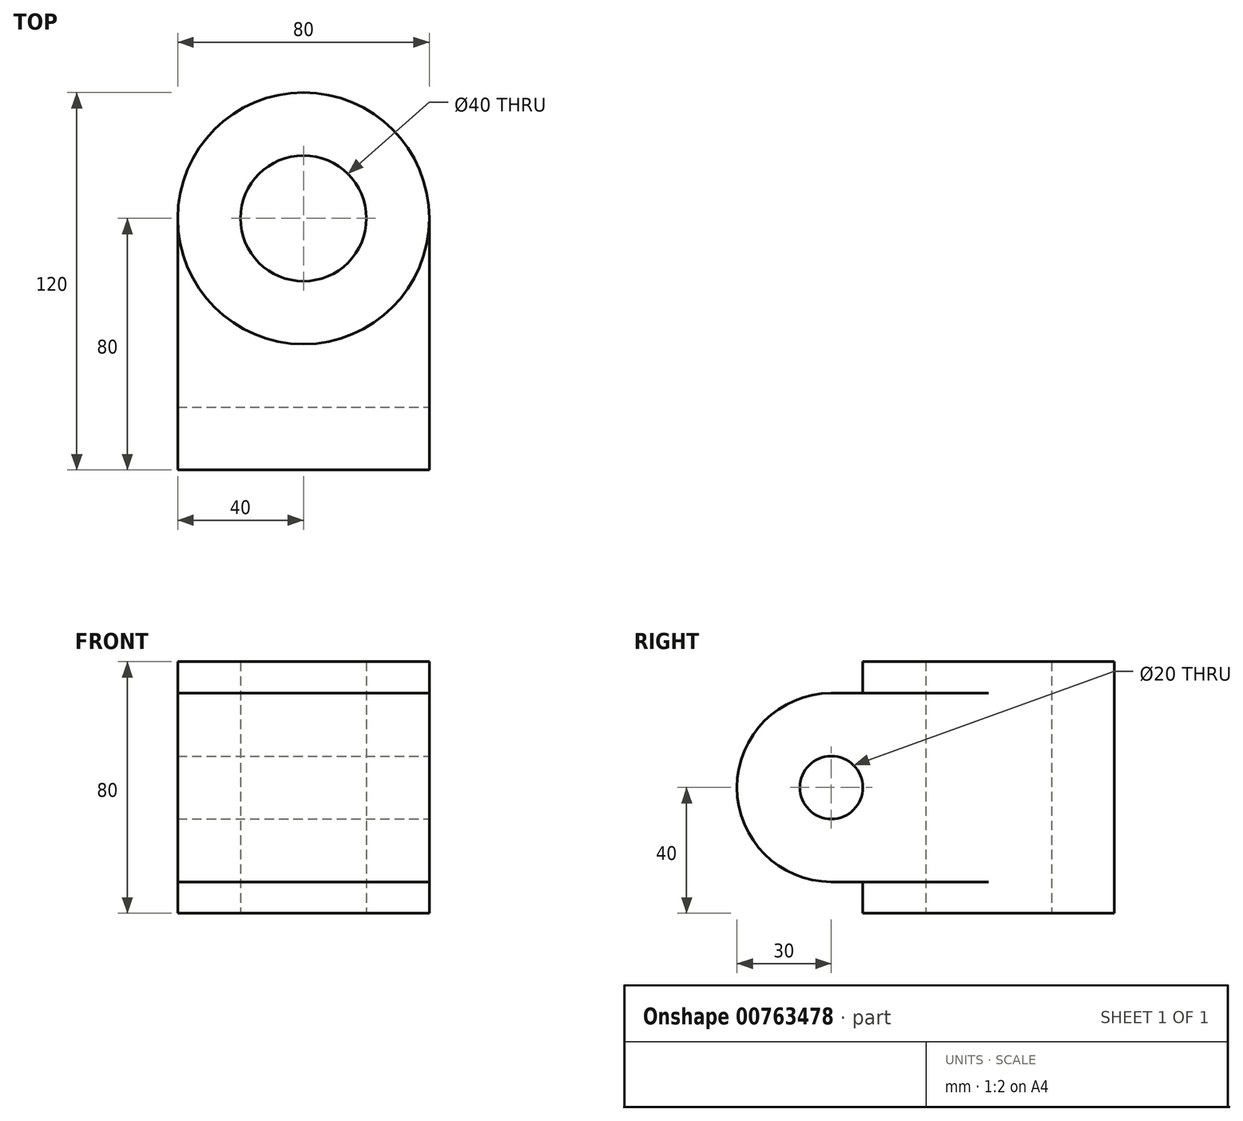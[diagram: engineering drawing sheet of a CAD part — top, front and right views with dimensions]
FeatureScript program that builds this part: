
annotation { "Feature Type Name" : "Feature", "Feature Type Description" : "" }
export const myFeature = defineFeature(function(context is Context, id is Id, definition is map)
    precondition{}
    {
        {
            var Q0;
            Q0=qCreatedBy(makeId("Top.planeOp"),FACE);
            var sketch = newSketch(context, id + "F0", { "sketchPlane" : qUnion([Q0])});
            skCircle(sketch, "E0", {"center": v(0, 0) * mm, "radius": 40 * mm});
            skCircle(sketch, "E1", {"center": v(0, 0) * mm, "radius": 20 * mm});
            skSolve(sketch);
        }
        {
            var Q0;
            Q0=makeQuery(id+"F0.imprint","IMPRINT",FACE,{"disambiguationData":[TD([[makeQuery(id+"F0.imprint","IMPRINT",EDGE,{"derivedFrom":sQuery(id+"F0.wireOp",EDGE,"E0")}),1.0]])]});
            extrude(context, id + "F1", {"entities" : qUnion([Q0]), "depth" : 80 * mm, "offsetDistance" : 25 * mm});
        }
        {
            var Q0;
            Q0=qCreatedBy(makeId("Right.planeOp"),FACE);
            var sketch = newSketch(context, id + "F2", { "sketchPlane" : qUnion([Q0])});
            skLineSegment(sketch, "E2.bottom", {"start": v(-80, 70) * mm, "end": v(0, 70) * mm});
            skLineSegment(sketch, "E2.top", {"start": v(-80, 10) * mm, "end": v(0, 10) * mm});
            skLineSegment(sketch, "E2.left", {"start": v(-80, 70) * mm, "end": v(-80, 10) * mm});
            skLineSegment(sketch, "E2.right", {"start": v(0, 70) * mm, "end": v(0, 10) * mm});
            skSolve(sketch);
        }
        {
            var Q0;
            Q0=makeQuery(id+"F2.imprint","IMPRINT",FACE,{"disambiguationData":[TD([[makeQuery(id+"F2.imprint","IMPRINT",EDGE,{"derivedFrom":sQuery(id+"F2.wireOp",EDGE,"E2.bottom")}),-1.0]])]});
            extrude(context, id + "F3", {"entities" : qUnion([Q0]), "operationType" : NewBodyOperationType.ADD, "endBound" : BoundingType.SYMMETRIC, "depth" : 80 * mm, "offsetDistance" : 25 * mm});
        }
        {
            var Q0;
            Q0=makeQuery(id+"F3.boolean.opBoolean","SPLIT",FACE,{"disambiguationData":[TD([makeQuery(id+"F1.opExtrude","SWEPT_FACE",FACE,{"disambiguationData":[OSD([sQuery(id+"F0.wireOp",EDGE,"E1")])]})])],"derivedFrom":makeQuery(id+"F3.opExtrude","SWEPT_FACE",FACE,{"disambiguationData":[OSD([sQuery(id+"F2.wireOp",EDGE,"E2.bottom")])]})});
            extrude(context, id + "F4", {"entities" : qUnion([Q0]), "operationType" : NewBodyOperationType.REMOVE, "endBound" : BoundingType.THROUGH_ALL, "oppositeDirection" : true, "depth" : 25 * mm, "offsetDistance" : 25 * mm});
        }
        {
            var Q0;
            Q0=makeQuery(id+"F3.opExtrude","SWEPT_EDGE",EDGE,{"disambiguationData":[OSD([sQuery(id+"F2.wireOp",EDGE,"E2.bottom"),sQuery(id+"F2.wireOp",EDGE,"E2.left")])]});
            var Q1;
            Q1=makeQuery(id+"F3.opExtrude","SWEPT_EDGE",EDGE,{"disambiguationData":[OSD([sQuery(id+"F2.wireOp",EDGE,"E2.top"),sQuery(id+"F2.wireOp",EDGE,"E2.left")])]});
            fillet(context, id + "F5", {"entities" : qUnion([Q0, Q1]), "radius" : 30 * mm, "tangentPropagation" : true, "allowEdgeOverflow" : false});
        }
        {
            var Q0;
            Q0=makeQuery(id+"F3.opExtrude","CAP_FACE",FACE,{"disambiguationData":[OSD([sQuery(id+"F2.wireOp",EDGE,"E2.bottom"),sQuery(id+"F2.wireOp",EDGE,"E2.top"),sQuery(id+"F2.wireOp",EDGE,"E2.left"),sQuery(id+"F2.wireOp",EDGE,"E2.right")])],"isStart":false});
            var sketch = newSketch(context, id + "F6", { "sketchPlane" : qUnion([Q0])});
            skCircle(sketch, "E3", {"center": v(-50, 40) * mm, "radius": 10 * mm});
            skSolve(sketch);
        }
        {
            var Q0;
            Q0=makeQuery(id+"F6.imprint","IMPRINT",FACE,{"disambiguationData":[TD([[makeQuery(id+"F6.imprint","IMPRINT",EDGE,{"derivedFrom":sQuery(id+"F6.wireOp",EDGE,"E3")}),1.0]])]});
            extrude(context, id + "F7", {"entities" : qUnion([Q0]), "operationType" : NewBodyOperationType.REMOVE, "endBound" : BoundingType.THROUGH_ALL, "oppositeDirection" : true, "depth" : 25 * mm, "offsetDistance" : 25 * mm});
        }
    });
